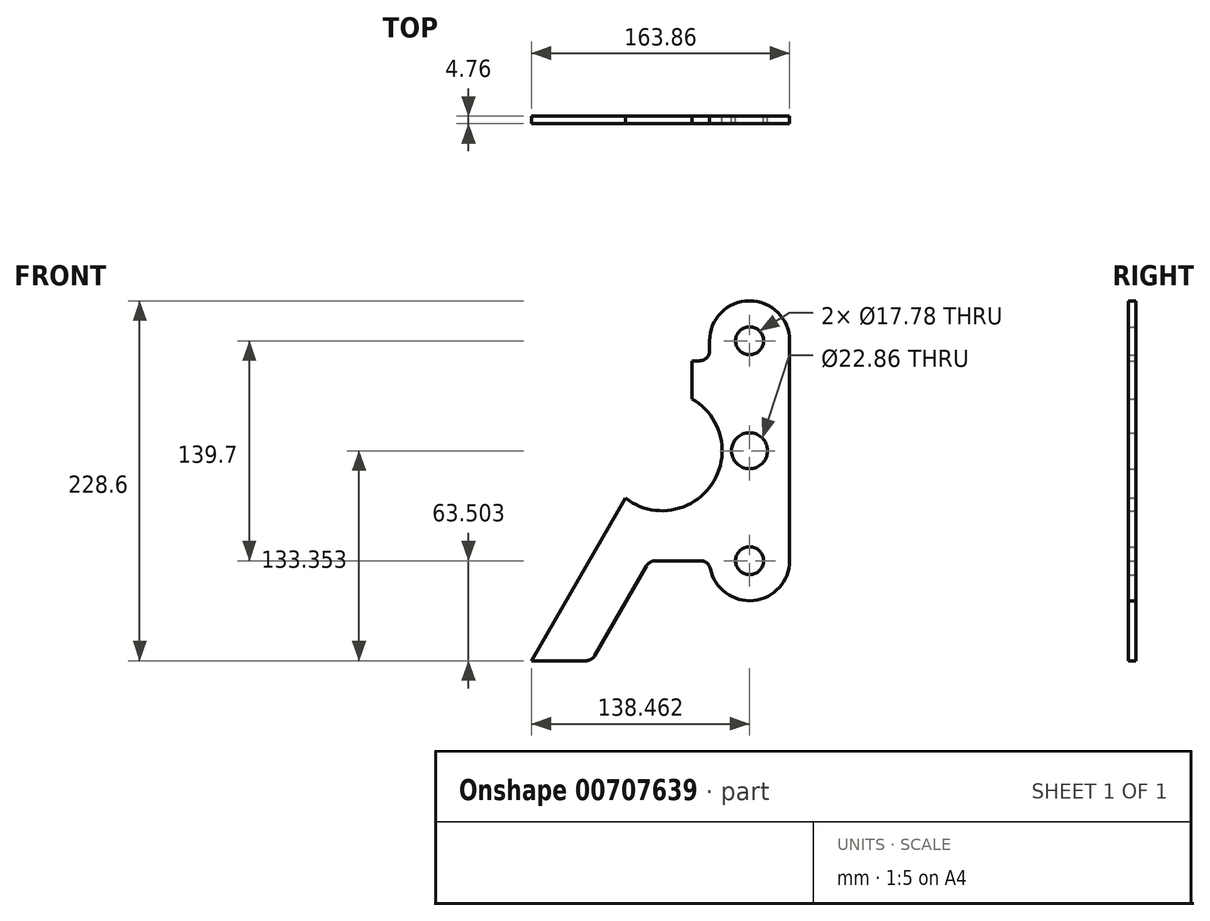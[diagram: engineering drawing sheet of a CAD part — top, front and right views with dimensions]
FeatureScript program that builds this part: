
annotation { "Feature Type Name" : "Feature", "Feature Type Description" : "" }
export const myFeature = defineFeature(function(context is Context, id is Id, definition is map)
    precondition{}
    {
        {
            var Q0;
            Q0=qCreatedBy(makeId("Front.planeOp"),FACE);
            var sketch = newSketch(context, id + "F0", { "sketchPlane" : qUnion([Q0])});
            skLineSegment(sketch, "E0", {"start": v(42.35, 87.26) * mm, "end": v(47.11, 87.26) * mm});
            skLineSegment(sketch, "E1", {"start": v(53.46, 93.61) * mm, "end": v(53.46, 99.96) * mm});
            skLineSegment(sketch, "E2", {"start": v(104.26, 99.96) * mm, "end": v(104.26, -39.74) * mm});
            skLineSegment(sketch, "E3", {"start": v(42.35, 87.26) * mm, "end": v(42.35, 63.13) * mm});
            skArc(sketch, "E4", {"start": v(42.35, 63.13) * mm, "mid": v(54.98, 8.89) * mm, "end": v(0, 0) * mm});
            skArc(sketch, "E5", {"start": v(53.46, 99.96) * mm, "mid": v(78.86, 125.36) * mm, "end": v(104.26, 99.96) * mm});
            skCircle(sketch, "E6", {"center": v(78.86, 99.96) * mm, "radius": 8.9 * mm});
            skArc(sketch, "E7.MirrorCS", {"start": v(53.98, -44.82) * mm, "mid": v(81.42, -65) * mm, "end": v(104.26, -39.74) * mm});
            skCircle(sketch, "E8.MirrorC", {"center": v(78.86, -39.74) * mm, "radius": 8.9 * mm});
            skLineSegment(sketch, "E9", {"start": v(47.75, -39.74) * mm, "end": v(19.03, -39.74) * mm});
            skLineSegment(sketch, "E10", {"start": v(13.53, -42.91) * mm, "end": v(-19.47, -100.06) * mm});
            skPoint(sketch, "E11.visualSharp", {"position": v(53.46, 87.26) * mm});
            skArc(sketch, "E11.filletArc", {"start": v(47.11, 87.26) * mm, "mid": v(51.6, 89.12) * mm, "end": v(53.46, 93.61) * mm});
            skPoint(sketch, "E12.visualSharp", {"position": v(53.46, -39.74) * mm});
            skArc(sketch, "E12.filletArc", {"start": v(53.98, -44.82) * mm, "mid": v(51.77, -41.17) * mm, "end": v(47.75, -39.74) * mm});
            skPoint(sketch, "E13.visualSharp", {"position": v(15.36, -39.74) * mm});
            skArc(sketch, "E13.filletArc", {"start": v(19.03, -39.74) * mm, "mid": v(15.85, -40.59) * mm, "end": v(13.53, -42.91) * mm});
            skLineSegment(sketch, "E14", {"start": v(0, 0) * mm, "end": v(-59.6, -103.24) * mm});
            skLineSegment(sketch, "E15", {"start": v(-59.6, -103.24) * mm, "end": v(-24.97, -103.24) * mm});
            skLineSegment(sketch, "E16", {"start": v(78.86, 125.36) * mm, "end": v(78.86, -65.14) * mm, "construction": true});
            skPoint(sketch, "E16.startSnap0", {"position": v(78.86, 125.36) * mm});
            skLineSegment(sketch, "E17", {"start": v(0, 0) * mm, "end": v(42.35, 63.13) * mm, "construction": true});
            skLineSegment(sketch, "E18", {"start": v(-87.11, 0) * mm, "end": v(123.45, 0) * mm, "construction": true});
            skPoint(sketch, "E19.visualSharp", {"position": v(-21.3, -103.24) * mm});
            skArc(sketch, "E19.filletArc", {"start": v(-24.97, -103.24) * mm, "mid": v(-21.8, -102.39) * mm, "end": v(-19.47, -100.06) * mm});
            skCircle(sketch, "E20", {"center": v(78.86, 30.11) * mm, "radius": 11.43 * mm});
            skSolve(sketch);
        }
        {
            var Q0;
            Q0=qSketchRegion(id+"F0",true);
            extrude(context, id + "F1", {"entities" : qUnion([Q0]), "depth" : 4.76 * mm, "offsetDistance" : 25.4 * mm});
        }
    });
